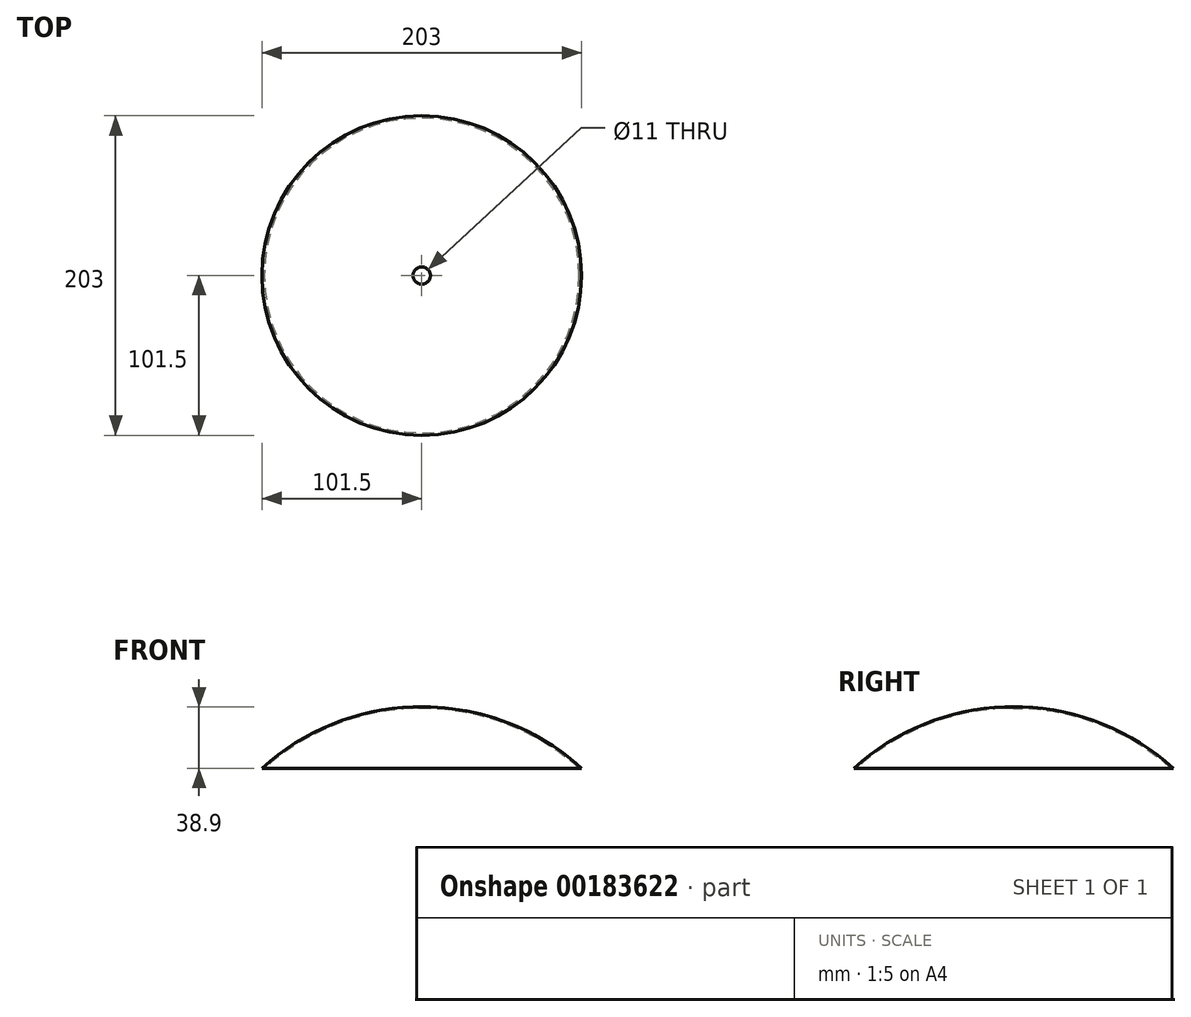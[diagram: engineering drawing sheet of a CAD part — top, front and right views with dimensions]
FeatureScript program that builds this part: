
annotation { "Feature Type Name" : "Feature", "Feature Type Description" : "" }
export const myFeature = defineFeature(function(context is Context, id is Id, definition is map)
    precondition{}
    {
        {
            var Q0;
            Q0=qCreatedBy(makeId("Front.planeOp"),FACE);
            var sketch = newSketch(context, id + "F0", { "sketchPlane" : qUnion([Q0])});
            skLineSegment(sketch, "E0.bottom", {"start": v(0, -19) * mm, "end": v(100, -19) * mm});
            skArc(sketch, "E1", {"start": v(100, -19) * mm, "mid": v(53.49, 9.18) * mm, "end": v(0, 19) * mm});
            skPoint(sketch, "E1.second.point", {"position": v(0, 19) * mm});
            skLineSegment(sketch, "E2", {"start": v(0, 19) * mm, "end": v(0, -19) * mm});
            skSolve(sketch);
        }
        {
            var Q0;
            Q0 = qSketchRegion(id + "F0", true);
            var Q1;
            Q1=sQuery(id+"F0.wireOp",EDGE,"E2");
            revolve(context, id + "F1", {"entities" : qUnion([Q0]), "axis" : qUnion([Q1]), "revolveType" : RevolveType.FULL});
        }
        {
            var Q0;
            Q0=makeQuery(id+"F1.opRevolve","SWEPT_FACE",FACE,{"disambiguationData":[OSD([sQuery(id+"F0.wireOp",EDGE,"E0.bottom")])]});
            shell(context, id + "F2", {"entities" : qUnion([Q0]), "thickness" : 1 * mm, "oppositeDirection" : true});
        }
        {
            var Q0;
            Q0=qCreatedBy(makeId("Top.planeOp"),FACE);
            var sketch = newSketch(context, id + "F3", { "sketchPlane" : qUnion([Q0])});
            skCircle(sketch, "E3", {"center": v(0, 0) * mm, "radius": 5.5 * mm});
            skSolve(sketch);
        }
        {
            var Q0;
            Q0 = qSketchRegion(id + "F3", true);
            extrude(context, id + "F4", {"entities" : qUnion([Q0]), "operationType" : NewBodyOperationType.REMOVE, "endBound" : BoundingType.THROUGH_ALL, "depth" : 25 * mm});
        }
    });
